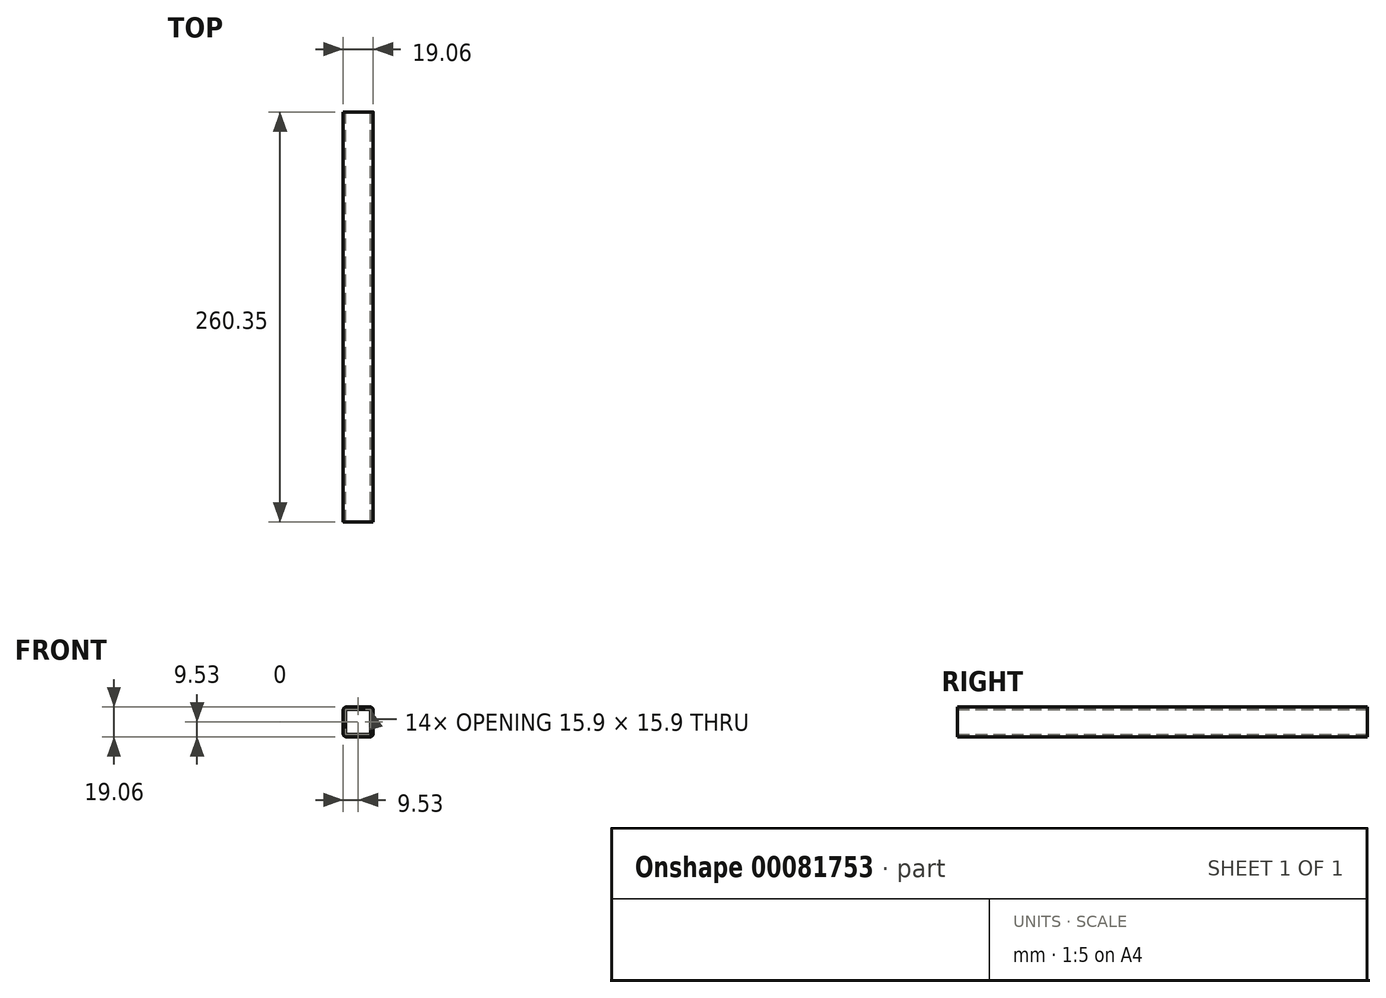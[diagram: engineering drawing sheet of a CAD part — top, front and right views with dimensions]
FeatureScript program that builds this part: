
annotation { "Feature Type Name" : "Feature", "Feature Type Description" : "" }
export const myFeature = defineFeature(function(context is Context, id is Id, definition is map)
    precondition{}
    {
        {
            var Q0;
            Q0=qCreatedBy(makeId("Front.planeOp"),FACE);
            var sketch = newSketch(context, id + "F0", { "sketchPlane" : qUnion([Q0])});
            skLineSegment(sketch, "E0.bottom", {"start": v(7.44, -9.52) * mm, "end": v(-7.44, -9.53) * mm});
            skLineSegment(sketch, "E0.top", {"start": v(7.44, 9.53) * mm, "end": v(-7.44, 9.52) * mm});
            skLineSegment(sketch, "E0.left", {"start": v(9.53, -7.44) * mm, "end": v(9.53, 7.44) * mm});
            skLineSegment(sketch, "E0.right", {"start": v(-9.53, -7.44) * mm, "end": v(-9.53, 7.44) * mm});
            skPoint(sketch, "E0.middle", {"position": v(0, 0) * mm});
            skLineSegment(sketch, "E1.bottom", {"start": v(7.44, -7.95) * mm, "end": v(-7.44, -7.95) * mm});
            skLineSegment(sketch, "E1.top", {"start": v(7.44, 7.95) * mm, "end": v(-7.44, 7.95) * mm});
            skLineSegment(sketch, "E1.left", {"start": v(7.95, -7.44) * mm, "end": v(7.95, 7.44) * mm});
            skLineSegment(sketch, "E1.right", {"start": v(-7.95, -7.44) * mm, "end": v(-7.95, 7.44) * mm});
            skPoint(sketch, "E2.visualSharp", {"position": v(-7.95, 7.95) * mm});
            skArc(sketch, "E2.filletArc", {"start": v(-7.44, 7.95) * mm, "mid": v(-7.8, 7.8) * mm, "end": v(-7.95, 7.44) * mm});
            skPoint(sketch, "E3.visualSharp", {"position": v(7.95, 7.95) * mm});
            skArc(sketch, "E3.filletArc", {"start": v(7.95, 7.44) * mm, "mid": v(7.8, 7.8) * mm, "end": v(7.44, 7.95) * mm});
            skPoint(sketch, "E4.visualSharp", {"position": v(7.95, -7.95) * mm});
            skArc(sketch, "E4.filletArc", {"start": v(7.44, -7.95) * mm, "mid": v(7.8, -7.8) * mm, "end": v(7.95, -7.44) * mm});
            skPoint(sketch, "E5.visualSharp", {"position": v(-7.95, -7.95) * mm});
            skArc(sketch, "E5.filletArc", {"start": v(-7.95, -7.44) * mm, "mid": v(-7.8, -7.8) * mm, "end": v(-7.44, -7.95) * mm});
            skPoint(sketch, "E6.visualSharp", {"position": v(9.53, 9.53) * mm});
            skArc(sketch, "E6.filletArc", {"start": v(9.53, 7.44) * mm, "mid": v(8.91, 8.91) * mm, "end": v(7.44, 9.53) * mm});
            skPoint(sketch, "E7.visualSharp", {"position": v(-9.53, 9.52) * mm});
            skArc(sketch, "E7.filletArc", {"start": v(-7.44, 9.53) * mm, "mid": v(-8.91, 8.91) * mm, "end": v(-9.53, 7.44) * mm});
            skPoint(sketch, "E8.visualSharp", {"position": v(-9.53, -9.53) * mm});
            skArc(sketch, "E8.filletArc", {"start": v(-9.53, -7.44) * mm, "mid": v(-8.91, -8.91) * mm, "end": v(-7.44, -9.52) * mm});
            skPoint(sketch, "E9.visualSharp", {"position": v(9.53, -9.52) * mm});
            skArc(sketch, "E9.filletArc", {"start": v(7.44, -9.52) * mm, "mid": v(8.91, -8.91) * mm, "end": v(9.52, -7.44) * mm});
            skSolve(sketch);
        }
        {
            var Q0;
            Q0 = qSketchRegion(id + "F0", true);
            extrude(context, id + "F1", {"entities" : qUnion([Q0]), "depth" : 260.35 * mm});
        }
    });
